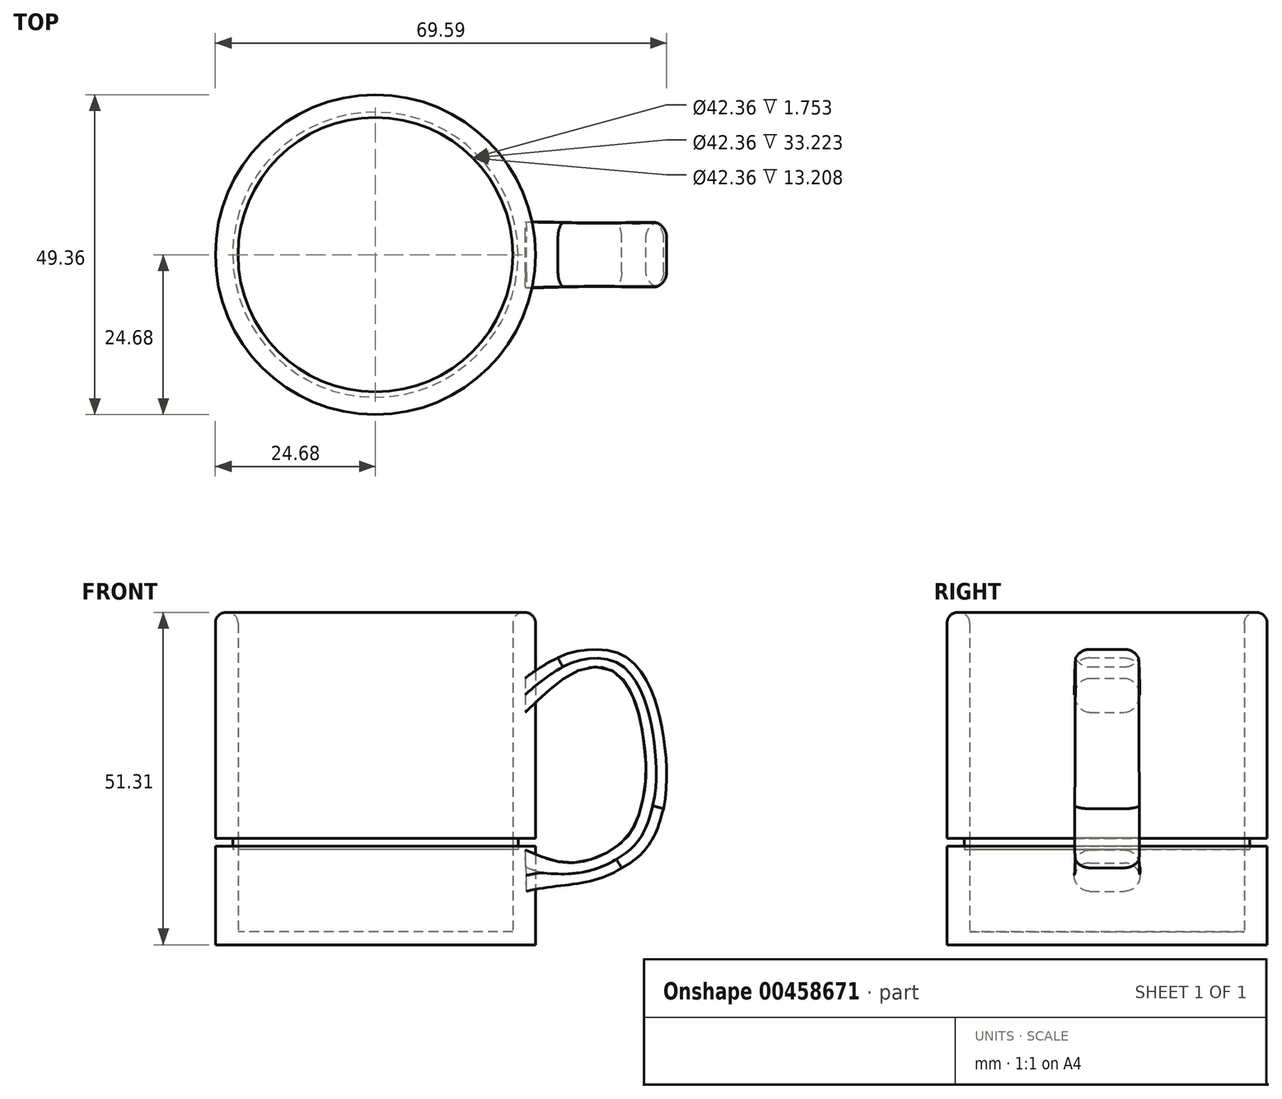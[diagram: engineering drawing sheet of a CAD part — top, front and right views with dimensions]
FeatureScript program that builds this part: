
annotation { "Feature Type Name" : "Feature", "Feature Type Description" : "" }
export const myFeature = defineFeature(function(context is Context, id is Id, definition is map)
    precondition{}
    {
        {
            var Q0;
            Q0=qCreatedBy(makeId("Top.planeOp"),FACE);
            var sketch = newSketch(context, id + "F0", { "sketchPlane" : qUnion([Q0])});
            skCircle(sketch, "E0", {"center": v(0, 0) * mm, "radius": 24.68 * mm});
            skCircle(sketch, "E1", {"center": v(0, 0) * mm, "radius": 21.18 * mm});
            skSolve(sketch);
        }
        {
            var Q0;
            Q0=makeQuery(id+"F0.imprint","IMPRINT",FACE,{"disambiguationData":[TD([[makeQuery(id+"F0.imprint","IMPRINT",EDGE,{"derivedFrom":sQuery(id+"F0.wireOp",EDGE,"E0")}),1.0]])]});
            extrude(context, id + "F1", {"entities" : qUnion([Q0]), "depth" : 15.24 * mm});
        }
        {
            var Q0;
            Q0=makeQuery(id+"F0.imprint","IMPRINT",FACE,{"disambiguationData":[TD([[makeQuery(id+"F0.imprint","IMPRINT",EDGE,{"derivedFrom":sQuery(id+"F0.wireOp",EDGE,"E1")}),1.0]])]});
            extrude(context, id + "F2", {"entities" : qUnion([Q0]), "operationType" : NewBodyOperationType.ADD, "depth" : 2.03 * mm});
        }
        {
            var Q0;
            Q0=makeQuery(id+"F0.imprint","IMPRINT",FACE,{"disambiguationData":[TD([[makeQuery(id+"F0.imprint","IMPRINT",EDGE,{"derivedFrom":sQuery(id+"F0.wireOp",EDGE,"E0")}),1.0]])]});
            extrude(context, id + "F3", {"entities" : qUnion([Q0]), "depth" : 51.3 * mm, "hasSecondDirection" : true, "secondDirectionOppositeDirection" : false, "secondDirectionDepth" : 16.4 * mm});
        }
        {
            var Q0;
            Q0=qCreatedBy(makeId("Top.planeOp"),FACE);
            var sketch = newSketch(context, id + "F4", { "sketchPlane" : qUnion([Q0])});
            skCircle(sketch, "E2", {"center": v(0, 0) * mm, "radius": 22 * mm});
            skCircle(sketch, "E3", {"center": v(0, 0) * mm, "radius": 21.18 * mm});
            skSolve(sketch);
        }
        {
            var Q0;
            Q0=makeQuery(id+"F4.imprint","IMPRINT",FACE,{"disambiguationData":[TD([[makeQuery(id+"F4.imprint","IMPRINT",EDGE,{"derivedFrom":sQuery(id+"F4.wireOp",EDGE,"E2")}),1.0]])]});
            extrude(context, id + "F5", {"entities" : qUnion([Q0]), "depth" : 16.48 * mm, "hasSecondDirection" : true, "secondDirectionOppositeDirection" : false, "secondDirectionDepth" : 14.73 * mm});
        }
        {
            var Q0;
            Q0=qCreatedBy(makeId("Front.planeOp"),FACE);
            var sketch = newSketch(context, id + "F6", { "sketchPlane" : qUnion([Q0])});
            skFitSpline(sketch, "E4", {"points": [v(23.08, 41.13) * mm, v(28.15, 44.27) * mm], "startDerivative": vector(3.12, 2.53) * mm, "endDerivative": vector(4.6, 1.91) * mm});
            skFitSpline(sketch, "E5", {"points": [v(28.15, 44.27) * mm, v(30.87, 45.26) * mm, v(35.04, 45.55) * mm, v(38.86, 44.27) * mm, v(41.96, 40.4) * mm, v(44.26, 33.04) * mm, v(44.43, 21) * mm], "startDerivative": vector(15.54, 10.45) * mm, "endDerivative": vector(-9.94, -43.11) * mm});
            skFitSpline(sketch, "E6", {"points": [v(37.96, 11.88) * mm, v(44.43, 21) * mm], "startDerivative": vector(15.28, 7.73) * mm, "endDerivative": vector(2.5, 7.76) * mm});
            skFitSpline(sketch, "E7", {"points": [v(37.96, 11.88) * mm, v(32.35, 9.65) * mm, v(23.3, 8.26) * mm], "startDerivative": vector(-8.62, -6.37) * mm, "endDerivative": vector(-17.75, -4.34) * mm});
            skFitSpline(sketch, "E8", {"points": [v(23.08, 35.83) * mm, v(28.53, 40.7) * mm, v(31.74, 42.48) * mm, v(35.17, 42.8) * mm, v(37.7, 41.41) * mm, v(39.47, 38.85) * mm, v(40.64, 35.55) * mm, v(41.2, 32.66) * mm, v(41.73, 26.63) * mm, v(41.15, 22.16) * mm, v(39.66, 17.82) * mm, v(35.97, 14.34) * mm, v(31.01, 12.68) * mm, v(23.08, 14.62) * mm], "startDerivative": vector(66.83, 66.18) * mm, "endDerivative": vector(-118.1, 50.87) * mm});
            skLineSegment(sketch, "E9", {"start": v(23.08, 41.13) * mm, "end": v(23.08, 35.83) * mm});
            skLineSegment(sketch, "E10", {"start": v(23.08, 14.62) * mm, "end": v(23.3, 8.26) * mm});
            skSolve(sketch);
        }
        {
            var Q0;
            Q0=makeQuery(id+"F6.imprint","IMPRINT",FACE,{"disambiguationData":[TD([[makeQuery(id+"F6.imprint","IMPRINT",EDGE,{"derivedFrom":sQuery(id+"F6.wireOp",EDGE,"E4")}),-1.0]])]});
            extrude(context, id + "F7", {"entities" : qUnion([Q0]), "depth" : 5.08 * mm, "hasSecondDirection" : true, "secondDirectionOppositeDirection" : true, "secondDirectionDepth" : 5.08 * mm});
        }
        {
            var Q0;
            Q0=makeQuery(id+"F7.opExtrude","CAP_EDGE",EDGE,{"disambiguationData":[OSD([sQuery(id+"F6.wireOp",EDGE,"E5")])],"isStart":false});
            var Q1;
            Q1=makeQuery(id+"F7.opExtrude","CAP_EDGE",EDGE,{"disambiguationData":[OSD([sQuery(id+"F6.wireOp",EDGE,"E6")])],"isStart":false});
            var Q2;
            Q2=makeQuery(id+"F7.opExtrude","CAP_EDGE",EDGE,{"disambiguationData":[OSD([sQuery(id+"F6.wireOp",EDGE,"E7")])],"isStart":false});
            var Q3;
            Q3=makeQuery(id+"F7.opExtrude","CAP_EDGE",EDGE,{"disambiguationData":[OSD([sQuery(id+"F6.wireOp",EDGE,"E8")])],"isStart":false});
            var Q4;
            Q4=makeQuery(id+"F7.opExtrude","CAP_EDGE",EDGE,{"disambiguationData":[OSD([sQuery(id+"F6.wireOp",EDGE,"E4")])],"isStart":false});
            fillet(context, id + "F8", {"entities" : qUnion([Q0, Q1, Q2, Q3, Q4]), "radius" : 2.4 * mm, "tangentPropagation" : true, "allowEdgeOverflow" : false});
        }
        {
            var Q0;
            Q0=makeQuery(id+"F7.opExtrude","CAP_EDGE",EDGE,{"disambiguationData":[OSD([sQuery(id+"F6.wireOp",EDGE,"E4")])],"isStart":true});
            var Q1;
            Q1=makeQuery(id+"F7.opExtrude","CAP_EDGE",EDGE,{"disambiguationData":[OSD([sQuery(id+"F6.wireOp",EDGE,"E5")])],"isStart":true});
            var Q2;
            Q2=makeQuery(id+"F7.opExtrude","CAP_EDGE",EDGE,{"disambiguationData":[OSD([sQuery(id+"F6.wireOp",EDGE,"E6")])],"isStart":true});
            var Q3;
            Q3=makeQuery(id+"F7.opExtrude","CAP_EDGE",EDGE,{"disambiguationData":[OSD([sQuery(id+"F6.wireOp",EDGE,"E7")])],"isStart":true});
            var Q4;
            Q4=makeQuery(id+"F7.opExtrude","CAP_EDGE",EDGE,{"disambiguationData":[OSD([sQuery(id+"F6.wireOp",EDGE,"E8")])],"isStart":true});
            fillet(context, id + "F9", {"entities" : qUnion([Q0, Q1, Q2, Q3, Q4]), "radius" : 2.4 * mm, "tangentPropagation" : true, "allowEdgeOverflow" : false});
        }
        {
            var Q0;
            Q0=qCreatedBy(makeId("Front.planeOp"),FACE);
            var sketch = newSketch(context, id + "F10", { "sketchPlane" : qUnion([Q0])});
            skLineSegment(sketch, "E11", {"start": v(-24.68, 15.24) * mm, "end": v(-24.95, 15.6) * mm});
            skSolve(sketch);
        }
        {
            var Q0;
            Q0=qCreatedBy(makeId("Front.planeOp"),FACE);
            var sketch = newSketch(context, id + "F11", { "sketchPlane" : qUnion([Q0])});
            skLineSegment(sketch, "E12", {"start": v(0, 0) * mm, "end": v(0, 4.23) * mm});
            skSolve(sketch);
        }
        {
            var Q0;
            Q0=sQuery(id+"F10.wireOp",EDGE,"E11");
            var Q1;
            Q1=sQuery(id+"F11.wireOp",EDGE,"E12");
            revolve(context, id + "F12", {"bodyType" : ToolBodyType.SURFACE, "surfaceEntities" : qUnion([Q0]), "axis" : qUnion([Q1]), "revolveType" : RevolveType.FULL});
        }
        {
            var Q0;
            Q0=makeQuery(id+"F3.opExtrude","CAP_EDGE",EDGE,{"disambiguationData":[OSD([sQuery(id+"F0.wireOp",EDGE,"E0")])],"isStart":false});
            fillet(context, id + "F13", {"entities" : qUnion([Q0]), "radius" : 1.68 * mm, "tangentPropagation" : true, "allowEdgeOverflow" : false});
        }
        {
            var Q0;
            Q0=makeQuery(id+"F3.opExtrude","CAP_EDGE",EDGE,{"disambiguationData":[OSD([sQuery(id+"F0.wireOp",EDGE,"E1")])],"isStart":false});
            fillet(context, id + "F14", {"entities" : qUnion([Q0]), "radius" : 1.68 * mm, "tangentPropagation" : true, "allowEdgeOverflow" : false});
        }
        {
            var Q0;
            Q0=makeQuery(id+"F2.opExtrude","CAP_FACE",FACE,{"disambiguationData":[OSD([sQuery(id+"F0.wireOp",EDGE,"E1")])],"isStart":false});
            var sketch = newSketch(context, id + "F15", { "sketchPlane" : qUnion([Q0])});
            skCircle(sketch, "E13", {"center": v(0, 0) * mm, "radius": 20.98 * mm});
            skSolve(sketch);
        }
        {
            var Q0;
            Q0=sQuery(id+"F15.wireOp",EDGE,"E13");
            extrude(context, id + "F16", {"bodyType" : ToolBodyType.SURFACE, "surfaceEntities" : qUnion([Q0]), "depth" : 47.65 * mm});
        }
    });
